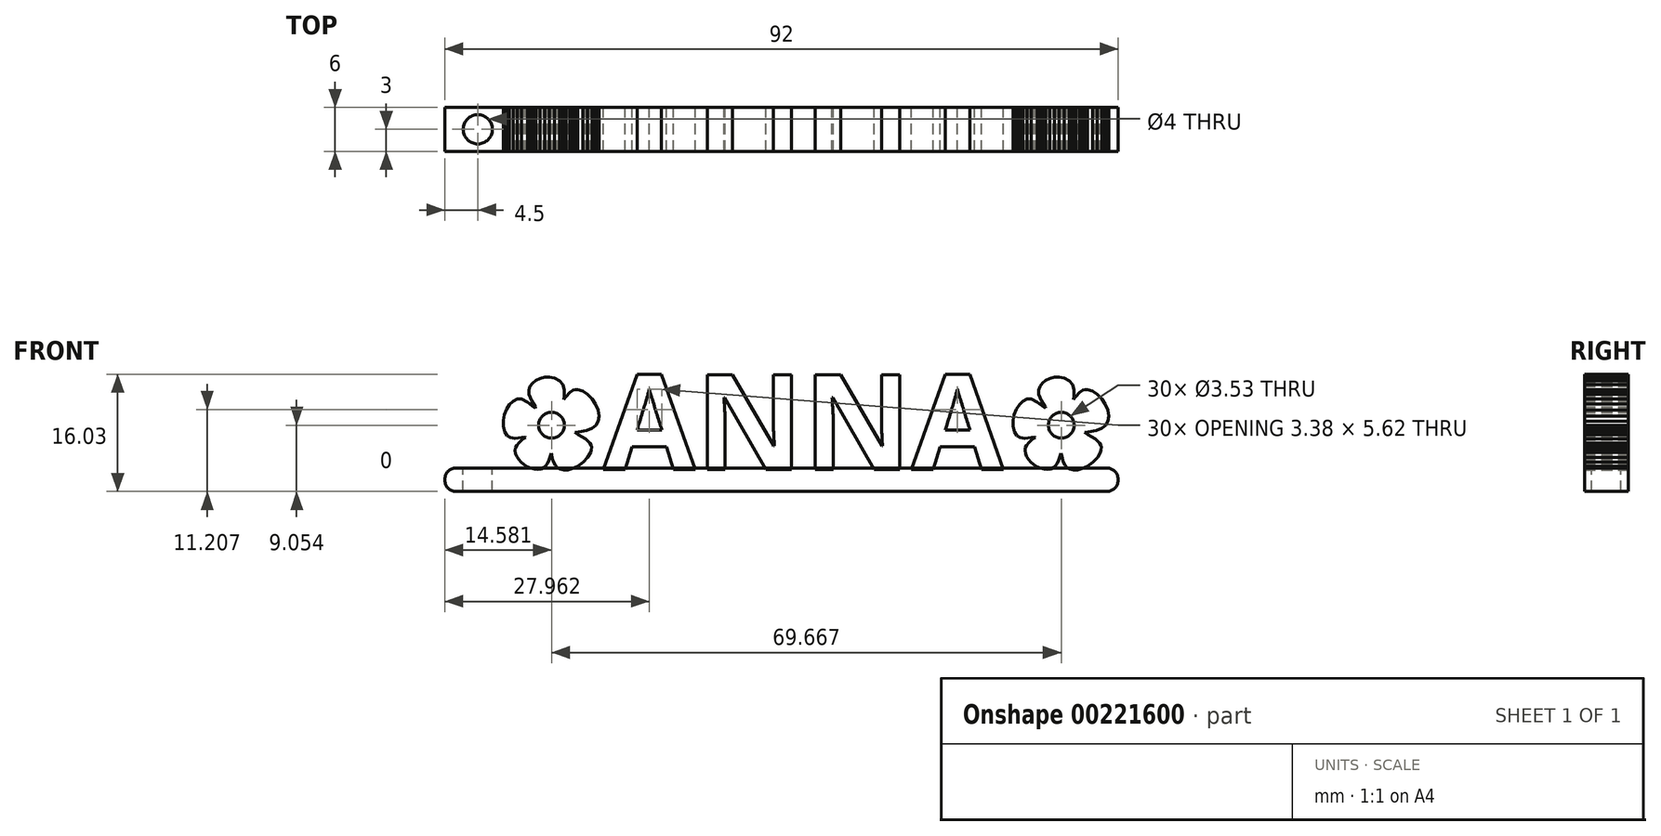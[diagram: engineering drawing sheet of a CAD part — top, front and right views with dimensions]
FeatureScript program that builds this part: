
annotation { "Feature Type Name" : "Feature", "Feature Type Description" : "" }
export const myFeature = defineFeature(function(context is Context, id is Id, definition is map)
    precondition{}
    {
        {
            var Q0;
            Q0=qCreatedBy(makeId("Front.planeOp"),FACE);
            var sketch = newSketch(context, id + "F0", { "sketchPlane" : qUnion([Q0])});
            skText(sketch, "E0", { "text": "   ANNA", "fontName": "OpenSans-Bold.ttf"});
            skLineSegment(sketch, "E1.0.0", {"start": v(-9.3, 0.1) * mm, "end": v(-8.53, 0.46) * mm});
            skLineSegment(sketch, "E1.0.1", {"start": v(-8.53, 0.46) * mm, "end": v(-7.79, 1.02) * mm});
            skLineSegment(sketch, "E1.0.2", {"start": v(-7.79, 1.02) * mm, "end": v(-7.18, 1.67) * mm});
            skLineSegment(sketch, "E1.0.3", {"start": v(-7.18, 1.67) * mm, "end": v(-6.78, 2.35) * mm});
            skLineSegment(sketch, "E1.0.4", {"start": v(-6.78, 2.35) * mm, "end": v(-6.68, 2.7) * mm});
            skLineSegment(sketch, "E1.0.5", {"start": v(-6.68, 2.7) * mm, "end": v(-6.67, 3.02) * mm});
            skLineSegment(sketch, "E1.0.6", {"start": v(-6.67, 3.02) * mm, "end": v(-6.73, 3.33) * mm});
            skLineSegment(sketch, "E1.0.7", {"start": v(-6.73, 3.33) * mm, "end": v(-6.89, 3.62) * mm});
            skLineSegment(sketch, "E1.0.8", {"start": v(-6.89, 3.62) * mm, "end": v(-7.48, 4.2) * mm});
            skLineSegment(sketch, "E1.0.9", {"start": v(-7.48, 4.2) * mm, "end": v(-8.5, 4.79) * mm});
            skLineSegment(sketch, "E1.0.10", {"start": v(-8.5, 4.79) * mm, "end": v(-8.93, 5.06) * mm});
            skLineSegment(sketch, "E1.0.11", {"start": v(-8.93, 5.06) * mm, "end": v(-8.42, 5.16) * mm});
            skLineSegment(sketch, "E1.0.12", {"start": v(-8.42, 5.16) * mm, "end": v(-7.31, 5.37) * mm});
            skLineSegment(sketch, "E1.0.13", {"start": v(-7.31, 5.37) * mm, "end": v(-6.55, 5.65) * mm});
            skLineSegment(sketch, "E1.0.14", {"start": v(-6.55, 5.65) * mm, "end": v(-6.05, 6.04) * mm});
            skLineSegment(sketch, "E1.0.15", {"start": v(-6.05, 6.04) * mm, "end": v(-5.76, 6.58) * mm});
            skLineSegment(sketch, "E1.0.16", {"start": v(-5.76, 6.58) * mm, "end": v(-5.64, 7.33) * mm});
            skLineSegment(sketch, "E1.0.17", {"start": v(-5.64, 7.33) * mm, "end": v(-5.78, 8.14) * mm});
            skLineSegment(sketch, "E1.0.18", {"start": v(-5.78, 8.14) * mm, "end": v(-6.1, 8.93) * mm});
            skLineSegment(sketch, "E1.0.19", {"start": v(-6.1, 8.93) * mm, "end": v(-6.6, 9.67) * mm});
            skLineSegment(sketch, "E1.0.20", {"start": v(-6.6, 9.67) * mm, "end": v(-7.2, 10.28) * mm});
            skLineSegment(sketch, "E1.0.21", {"start": v(-7.2, 10.28) * mm, "end": v(-7.86, 10.72) * mm});
            skLineSegment(sketch, "E1.0.22", {"start": v(-7.86, 10.72) * mm, "end": v(-8.55, 10.93) * mm});
            skLineSegment(sketch, "E1.0.23", {"start": v(-8.55, 10.93) * mm, "end": v(-8.88, 10.93) * mm});
            skLineSegment(sketch, "E1.0.24", {"start": v(-8.88, 10.93) * mm, "end": v(-9.2, 10.85) * mm});
            skLineSegment(sketch, "E1.0.25", {"start": v(-9.2, 10.85) * mm, "end": v(-9.65, 10.56) * mm});
            skLineSegment(sketch, "E1.0.26", {"start": v(-9.65, 10.56) * mm, "end": v(-10.14, 9.98) * mm});
            skLineSegment(sketch, "E1.0.27", {"start": v(-10.14, 9.98) * mm, "end": v(-10.45, 9.58) * mm});
            skLineSegment(sketch, "E1.0.28", {"start": v(-10.45, 9.58) * mm, "end": v(-10.4, 10.03) * mm});
            skLineSegment(sketch, "E1.0.29", {"start": v(-10.4, 10.03) * mm, "end": v(-10.4, 10.93) * mm});
            skLineSegment(sketch, "E1.0.30", {"start": v(-10.4, 10.93) * mm, "end": v(-10.6, 11.63) * mm});
            skLineSegment(sketch, "E1.0.31", {"start": v(-10.6, 11.63) * mm, "end": v(-11.04, 12.15) * mm});
            skLineSegment(sketch, "E1.0.32", {"start": v(-11.04, 12.15) * mm, "end": v(-11.71, 12.5) * mm});
            skLineSegment(sketch, "E1.0.33", {"start": v(-11.71, 12.5) * mm, "end": v(-12.4, 12.64) * mm});
            skLineSegment(sketch, "E1.0.34", {"start": v(-12.4, 12.64) * mm, "end": v(-13.07, 12.62) * mm});
            skLineSegment(sketch, "E1.0.35", {"start": v(-13.07, 12.62) * mm, "end": v(-13.7, 12.47) * mm});
            skLineSegment(sketch, "E1.0.36", {"start": v(-13.7, 12.47) * mm, "end": v(-14.26, 12.2) * mm});
            skLineSegment(sketch, "E1.0.37", {"start": v(-14.26, 12.2) * mm, "end": v(-14.72, 11.83) * mm});
            skLineSegment(sketch, "E1.0.38", {"start": v(-14.72, 11.83) * mm, "end": v(-15.05, 11.38) * mm});
            skLineSegment(sketch, "E1.0.39", {"start": v(-15.05, 11.38) * mm, "end": v(-15.22, 10.87) * mm});
            skLineSegment(sketch, "E1.0.40", {"start": v(-15.22, 10.87) * mm, "end": v(-15.2, 10.3) * mm});
            skLineSegment(sketch, "E1.0.41", {"start": v(-15.2, 10.3) * mm, "end": v(-14.83, 9.4) * mm});
            skLineSegment(sketch, "E1.0.42", {"start": v(-14.83, 9.4) * mm, "end": v(-14.35, 8.55) * mm});
            skLineSegment(sketch, "E1.0.43", {"start": v(-14.35, 8.55) * mm, "end": v(-14.3, 8.4) * mm});
            skLineSegment(sketch, "E1.0.44", {"start": v(-14.3, 8.4) * mm, "end": v(-14.48, 8.53) * mm});
            skLineSegment(sketch, "E1.0.45", {"start": v(-14.48, 8.53) * mm, "end": v(-15.4, 9.23) * mm});
            skLineSegment(sketch, "E1.0.46", {"start": v(-15.4, 9.23) * mm, "end": v(-16.22, 9.63) * mm});
            skLineSegment(sketch, "E1.0.47", {"start": v(-16.22, 9.63) * mm, "end": v(-16.8, 9.63) * mm});
            skLineSegment(sketch, "E1.0.48", {"start": v(-16.8, 9.63) * mm, "end": v(-17.36, 9.37) * mm});
            skLineSegment(sketch, "E1.0.49", {"start": v(-17.36, 9.37) * mm, "end": v(-17.85, 8.9) * mm});
            skLineSegment(sketch, "E1.0.50", {"start": v(-17.85, 8.9) * mm, "end": v(-18.26, 8.26) * mm});
            skLineSegment(sketch, "E1.0.51", {"start": v(-18.26, 8.26) * mm, "end": v(-18.56, 7.51) * mm});
            skLineSegment(sketch, "E1.0.52", {"start": v(-18.56, 7.51) * mm, "end": v(-18.72, 6.71) * mm});
            skLineSegment(sketch, "E1.0.53", {"start": v(-18.72, 6.71) * mm, "end": v(-18.72, 5.9) * mm});
            skLineSegment(sketch, "E1.0.54", {"start": v(-18.72, 5.9) * mm, "end": v(-18.52, 5.16) * mm});
            skLineSegment(sketch, "E1.0.55", {"start": v(-18.52, 5.16) * mm, "end": v(-18.2, 4.64) * mm});
            skLineSegment(sketch, "E1.0.56", {"start": v(-18.2, 4.64) * mm, "end": v(-17.75, 4.36) * mm});
            skLineSegment(sketch, "E1.0.57", {"start": v(-17.75, 4.36) * mm, "end": v(-17.1, 4.27) * mm});
            skLineSegment(sketch, "E1.0.58", {"start": v(-17.1, 4.27) * mm, "end": v(-16.21, 4.37) * mm});
            skLineSegment(sketch, "E1.0.59", {"start": v(-16.21, 4.37) * mm, "end": v(-15.7, 4.43) * mm});
            skLineSegment(sketch, "E1.0.60", {"start": v(-15.7, 4.43) * mm, "end": v(-15.67, 4.4) * mm});
            skLineSegment(sketch, "E1.0.61", {"start": v(-15.67, 4.4) * mm, "end": v(-15.78, 4.33) * mm});
            skLineSegment(sketch, "E1.0.62", {"start": v(-15.78, 4.33) * mm, "end": v(-16.17, 4.07) * mm});
            skLineSegment(sketch, "E1.0.63", {"start": v(-16.17, 4.07) * mm, "end": v(-16.55, 3.71) * mm});
            skLineSegment(sketch, "E1.0.64", {"start": v(-16.55, 3.71) * mm, "end": v(-16.87, 3.33) * mm});
            skLineSegment(sketch, "E1.0.65", {"start": v(-16.87, 3.33) * mm, "end": v(-17.04, 3) * mm});
            skLineSegment(sketch, "E1.0.66", {"start": v(-17.04, 3) * mm, "end": v(-17.08, 2.6) * mm});
            skLineSegment(sketch, "E1.0.67", {"start": v(-17.08, 2.6) * mm, "end": v(-17.02, 2.2) * mm});
            skLineSegment(sketch, "E1.0.68", {"start": v(-17.02, 2.2) * mm, "end": v(-16.87, 1.78) * mm});
            skLineSegment(sketch, "E1.0.69", {"start": v(-16.87, 1.78) * mm, "end": v(-16.62, 1.39) * mm});
            skLineSegment(sketch, "E1.0.70", {"start": v(-16.62, 1.39) * mm, "end": v(-16.3, 1.02) * mm});
            skLineSegment(sketch, "E1.0.71", {"start": v(-16.3, 1.02) * mm, "end": v(-15.9, 0.69) * mm});
            skLineSegment(sketch, "E1.0.72", {"start": v(-15.9, 0.69) * mm, "end": v(-15.45, 0.4) * mm});
            skLineSegment(sketch, "E1.0.73", {"start": v(-15.45, 0.4) * mm, "end": v(-14.95, 0.2) * mm});
            skLineSegment(sketch, "E1.0.74", {"start": v(-14.95, 0.2) * mm, "end": v(-14.44, 0.06) * mm});
            skLineSegment(sketch, "E1.0.75", {"start": v(-14.44, 0.06) * mm, "end": v(-13.98, 0.02) * mm});
            skLineSegment(sketch, "E1.0.76", {"start": v(-13.98, 0.02) * mm, "end": v(-13.58, 0.08) * mm});
            skLineSegment(sketch, "E1.0.77", {"start": v(-13.58, 0.08) * mm, "end": v(-13.23, 0.23) * mm});
            skLineSegment(sketch, "E1.0.78", {"start": v(-13.23, 0.23) * mm, "end": v(-12.92, 0.49) * mm});
            skLineSegment(sketch, "E1.0.79", {"start": v(-12.92, 0.49) * mm, "end": v(-12.67, 0.84) * mm});
            skLineSegment(sketch, "E1.0.80", {"start": v(-12.67, 0.84) * mm, "end": v(-12.46, 1.28) * mm});
            skLineSegment(sketch, "E1.0.81", {"start": v(-12.46, 1.28) * mm, "end": v(-12.3, 1.83) * mm});
            skLineSegment(sketch, "E1.0.82", {"start": v(-12.3, 1.83) * mm, "end": v(-12.19, 2.26) * mm});
            skLineSegment(sketch, "E1.0.83", {"start": v(-12.19, 2.26) * mm, "end": v(-12.13, 2.1) * mm});
            skLineSegment(sketch, "E1.0.84", {"start": v(-12.13, 2.1) * mm, "end": v(-12.01, 1.53) * mm});
            skLineSegment(sketch, "E1.0.85", {"start": v(-12.01, 1.53) * mm, "end": v(-11.82, 1) * mm});
            skLineSegment(sketch, "E1.0.86", {"start": v(-11.82, 1) * mm, "end": v(-11.6, 0.55) * mm});
            skLineSegment(sketch, "E1.0.87", {"start": v(-11.6, 0.55) * mm, "end": v(-11.35, 0.26) * mm});
            skLineSegment(sketch, "E1.0.88", {"start": v(-11.35, 0.26) * mm, "end": v(-10.95, 0.05) * mm});
            skLineSegment(sketch, "E1.0.89", {"start": v(-10.95, 0.05) * mm, "end": v(-10.46, -0.04) * mm});
            skLineSegment(sketch, "E1.0.90", {"start": v(-10.46, -0.04) * mm, "end": v(-9.9, -0.03) * mm});
            skLineSegment(sketch, "E1.0.91", {"start": v(-9.9, -0.03) * mm, "end": v(-9.3, 0.1) * mm});
            skCircle(sketch, "E2", {"center": v(-12.12, 6.05) * mm, "radius": 1.77 * mm});
            skCircle(sketch, "E3.1.0.0", {"center": v(57.55, 6.05) * mm, "radius": 1.77 * mm});
            skLineSegment(sketch, "E3.1.0.1", {"start": v(59.22, 9.58) * mm, "end": v(59.26, 10.03) * mm});
            skLineSegment(sketch, "E3.1.0.2", {"start": v(62.47, 10.28) * mm, "end": v(61.8, 10.72) * mm});
            skLineSegment(sketch, "E3.1.0.3", {"start": v(50.95, 5.9) * mm, "end": v(51.15, 5.16) * mm});
            skLineSegment(sketch, "E3.1.0.4", {"start": v(55.4, 12.2) * mm, "end": v(54.94, 11.83) * mm});
            skLineSegment(sketch, "E3.1.0.5", {"start": v(53.37, 1.02) * mm, "end": v(53.76, 0.69) * mm});
            skLineSegment(sketch, "E3.1.0.6", {"start": v(53.45, 9.63) * mm, "end": v(52.86, 9.63) * mm});
            skLineSegment(sketch, "E3.1.0.7", {"start": v(51.1, 7.51) * mm, "end": v(50.95, 6.71) * mm});
            skLineSegment(sketch, "E3.1.0.8", {"start": v(54.27, 9.23) * mm, "end": v(53.45, 9.63) * mm});
            skLineSegment(sketch, "E3.1.0.9", {"start": v(52.86, 9.63) * mm, "end": v(52.31, 9.37) * mm});
            skLineSegment(sketch, "E3.1.0.10", {"start": v(59.53, 9.98) * mm, "end": v(59.22, 9.58) * mm});
            skLineSegment(sketch, "E3.1.0.11", {"start": v(59.07, 11.63) * mm, "end": v(58.63, 12.15) * mm});
            skLineSegment(sketch, "E3.1.0.12", {"start": v(58.63, 12.15) * mm, "end": v(57.95, 12.5) * mm});
            skLineSegment(sketch, "E3.1.0.13", {"start": v(59.28, 10.93) * mm, "end": v(59.07, 11.63) * mm});
            skLineSegment(sketch, "E3.1.0.14", {"start": v(54.21, 0.4) * mm, "end": v(54.72, 0.2) * mm});
            skLineSegment(sketch, "E3.1.0.15", {"start": v(59.77, -0.03) * mm, "end": v(60.36, 0.1) * mm});
            skLineSegment(sketch, "E3.1.0.16", {"start": v(50.95, 6.71) * mm, "end": v(50.95, 5.9) * mm});
            skLineSegment(sketch, "E3.1.0.17", {"start": v(60.36, 0.1) * mm, "end": v(61.14, 0.46) * mm});
            skLineSegment(sketch, "E3.1.0.18", {"start": v(53.76, 0.69) * mm, "end": v(54.21, 0.4) * mm});
            skLineSegment(sketch, "E3.1.0.19", {"start": v(51.15, 5.16) * mm, "end": v(51.47, 4.64) * mm});
            skLineSegment(sketch, "E3.1.0.20", {"start": v(62.35, 5.37) * mm, "end": v(63.12, 5.65) * mm});
            skLineSegment(sketch, "E3.1.0.21", {"start": v(61.14, 0.46) * mm, "end": v(61.88, 1.02) * mm});
            skLineSegment(sketch, "E3.1.0.22", {"start": v(63.07, 9.67) * mm, "end": v(62.47, 10.28) * mm});
            skLineSegment(sketch, "E3.1.0.23", {"start": v(59.26, 10.03) * mm, "end": v(59.28, 10.93) * mm});
            skLineSegment(sketch, "E3.1.0.24", {"start": v(52.31, 9.37) * mm, "end": v(51.81, 8.9) * mm});
            skLineSegment(sketch, "E3.1.0.25", {"start": v(57.95, 12.5) * mm, "end": v(57.27, 12.64) * mm});
            skLineSegment(sketch, "E3.1.0.26", {"start": v(56.6, 12.62) * mm, "end": v(55.96, 12.47) * mm});
            skLineSegment(sketch, "E3.1.0.27", {"start": v(62.5, 1.67) * mm, "end": v(62.88, 2.35) * mm});
            skLineSegment(sketch, "E3.1.0.28", {"start": v(63.56, 8.93) * mm, "end": v(63.07, 9.67) * mm});
            skLineSegment(sketch, "E3.1.0.29", {"start": v(57.27, 12.64) * mm, "end": v(56.6, 12.62) * mm});
            skLineSegment(sketch, "E3.1.0.30", {"start": v(61.88, 1.02) * mm, "end": v(62.5, 1.67) * mm});
            skLineSegment(sketch, "E3.1.0.31", {"start": v(51.81, 8.9) * mm, "end": v(51.4, 8.26) * mm});
            skLineSegment(sketch, "E3.1.0.32", {"start": v(51.4, 8.26) * mm, "end": v(51.1, 7.51) * mm});
            skLineSegment(sketch, "E3.1.0.33", {"start": v(55.96, 12.47) * mm, "end": v(55.4, 12.2) * mm});
            skLineSegment(sketch, "E3.1.0.34", {"start": v(62.88, 2.35) * mm, "end": v(62.98, 2.7) * mm});
            skLineSegment(sketch, "E3.1.0.35", {"start": v(52.86, 9.63) * mm, "end": v(52.31, 9.37) * mm});
            skLineSegment(sketch, "E3.1.0.36", {"start": v(57.27, 12.64) * mm, "end": v(56.6, 12.62) * mm});
            skLineSegment(sketch, "E3.1.0.37", {"start": v(62.35, 5.37) * mm, "end": v(63.12, 5.65) * mm});
            skLineSegment(sketch, "E3.1.0.38", {"start": v(58.71, 0.05) * mm, "end": v(59.21, -0.04) * mm});
            skLineSegment(sketch, "E3.1.0.39", {"start": v(63.56, 8.93) * mm, "end": v(63.07, 9.67) * mm});
            skLineSegment(sketch, "E3.1.0.40", {"start": v(59.77, -0.03) * mm, "end": v(60.36, 0.1) * mm});
            skLineSegment(sketch, "E3.1.0.41", {"start": v(59.53, 9.98) * mm, "end": v(59.22, 9.58) * mm});
            skLineSegment(sketch, "E3.1.0.42", {"start": v(61.88, 1.02) * mm, "end": v(62.5, 1.67) * mm});
            skLineSegment(sketch, "E3.1.0.43", {"start": v(62.88, 2.35) * mm, "end": v(62.98, 2.7) * mm});
            skLineSegment(sketch, "E3.1.0.44", {"start": v(50.95, 6.71) * mm, "end": v(50.95, 5.9) * mm});
            skLineSegment(sketch, "E3.1.0.45", {"start": v(60.36, 0.1) * mm, "end": v(61.14, 0.46) * mm});
            skLineSegment(sketch, "E3.1.0.46", {"start": v(56.6, 12.62) * mm, "end": v(55.96, 12.47) * mm});
            skLineSegment(sketch, "E3.1.0.47", {"start": v(55.4, 12.2) * mm, "end": v(54.94, 11.83) * mm});
            skLineSegment(sketch, "E3.1.0.48", {"start": v(54.21, 0.4) * mm, "end": v(54.72, 0.2) * mm});
            skLineSegment(sketch, "E3.1.0.49", {"start": v(59.26, 10.03) * mm, "end": v(59.28, 10.93) * mm});
            skLineSegment(sketch, "E3.1.0.50", {"start": v(59.22, 9.58) * mm, "end": v(59.26, 10.03) * mm});
            skLineSegment(sketch, "E3.1.0.51", {"start": v(59.21, -0.04) * mm, "end": v(59.77, -0.03) * mm});
            skLineSegment(sketch, "E3.1.0.52", {"start": v(53.45, 9.63) * mm, "end": v(52.86, 9.63) * mm});
            skLineSegment(sketch, "E3.1.0.53", {"start": v(59.28, 10.93) * mm, "end": v(59.07, 11.63) * mm});
            skLineSegment(sketch, "E3.1.0.54", {"start": v(62.47, 10.28) * mm, "end": v(61.8, 10.72) * mm});
            skLineSegment(sketch, "E3.1.0.55", {"start": v(51.81, 8.9) * mm, "end": v(51.4, 8.26) * mm});
            skLineSegment(sketch, "E3.1.0.56", {"start": v(53.76, 0.69) * mm, "end": v(54.21, 0.4) * mm});
            skLineSegment(sketch, "E3.1.0.57", {"start": v(57.95, 12.5) * mm, "end": v(57.27, 12.64) * mm});
            skLineSegment(sketch, "E3.1.0.58", {"start": v(52.31, 9.37) * mm, "end": v(51.81, 8.9) * mm});
            skLineSegment(sketch, "E3.1.0.59", {"start": v(50.95, 5.9) * mm, "end": v(51.15, 5.16) * mm});
            skLineSegment(sketch, "E3.1.0.60", {"start": v(58.63, 12.15) * mm, "end": v(57.95, 12.5) * mm});
            skLineSegment(sketch, "E3.1.0.61", {"start": v(54.27, 9.23) * mm, "end": v(53.45, 9.63) * mm});
            skLineSegment(sketch, "E3.1.0.62", {"start": v(61.14, 0.46) * mm, "end": v(61.88, 1.02) * mm});
            skLineSegment(sketch, "E3.1.0.63", {"start": v(59.07, 11.63) * mm, "end": v(58.63, 12.15) * mm});
            skLineSegment(sketch, "E3.1.0.64", {"start": v(51.4, 8.26) * mm, "end": v(51.1, 7.51) * mm});
            skLineSegment(sketch, "E3.1.0.65", {"start": v(62.5, 1.67) * mm, "end": v(62.88, 2.35) * mm});
            skLineSegment(sketch, "E3.1.0.66", {"start": v(51.1, 7.51) * mm, "end": v(50.95, 6.71) * mm});
            skLineSegment(sketch, "E3.1.0.67", {"start": v(53.37, 1.02) * mm, "end": v(53.76, 0.69) * mm});
            skLineSegment(sketch, "E3.1.0.68", {"start": v(51.15, 5.16) * mm, "end": v(51.47, 4.64) * mm});
            skLineSegment(sketch, "E3.1.0.69", {"start": v(55.96, 12.47) * mm, "end": v(55.4, 12.2) * mm});
            skLineSegment(sketch, "E3.1.0.70", {"start": v(63.07, 9.67) * mm, "end": v(62.47, 10.28) * mm});
            skLineSegment(sketch, "E3.1.0.71", {"start": v(54.94, 11.83) * mm, "end": v(54.61, 11.38) * mm});
            skLineSegment(sketch, "E3.1.0.72", {"start": v(61.8, 10.72) * mm, "end": v(61.12, 10.93) * mm});
            skLineSegment(sketch, "E3.1.0.73", {"start": v(63.61, 6.04) * mm, "end": v(63.91, 6.58) * mm});
            skLineSegment(sketch, "E3.1.0.74", {"start": v(62.98, 2.7) * mm, "end": v(63, 3.02) * mm});
            skLineSegment(sketch, "E3.1.0.75", {"start": v(61.12, 10.93) * mm, "end": v(60.79, 10.93) * mm});
            skLineSegment(sketch, "E3.1.0.76", {"start": v(51.47, 4.64) * mm, "end": v(51.92, 4.36) * mm});
            skLineSegment(sketch, "E3.1.0.77", {"start": v(60.46, 10.85) * mm, "end": v(60.02, 10.56) * mm});
            skLineSegment(sketch, "E3.1.0.78", {"start": v(61.25, 5.16) * mm, "end": v(62.35, 5.37) * mm});
            skLineSegment(sketch, "E3.1.0.79", {"start": v(63, 3.02) * mm, "end": v(62.94, 3.33) * mm});
            skLineSegment(sketch, "E3.1.0.80", {"start": v(62.94, 3.33) * mm, "end": v(62.78, 3.62) * mm});
            skLineSegment(sketch, "E3.1.0.81", {"start": v(62.18, 4.2) * mm, "end": v(61.17, 4.79) * mm});
            skLineSegment(sketch, "E3.1.0.82", {"start": v(64.02, 7.33) * mm, "end": v(63.9, 8.14) * mm});
            skLineSegment(sketch, "E3.1.0.83", {"start": v(53.04, 1.39) * mm, "end": v(53.37, 1.02) * mm});
            skLineSegment(sketch, "E3.1.0.84", {"start": v(55.23, 0.06) * mm, "end": v(55.68, 0.02) * mm});
            skLineSegment(sketch, "E3.1.0.85", {"start": v(60.74, 5.06) * mm, "end": v(61.25, 5.16) * mm});
            skLineSegment(sketch, "E3.1.0.86", {"start": v(58.31, 0.26) * mm, "end": v(58.71, 0.05) * mm});
            skLineSegment(sketch, "E3.1.0.87", {"start": v(54.61, 11.38) * mm, "end": v(54.45, 10.87) * mm});
            skLineSegment(sketch, "E3.1.0.88", {"start": v(63.91, 6.58) * mm, "end": v(64.02, 7.33) * mm});
            skLineSegment(sketch, "E3.1.0.89", {"start": v(58.71, 0.05) * mm, "end": v(59.21, -0.04) * mm});
            skLineSegment(sketch, "E3.1.0.90", {"start": v(61.17, 4.79) * mm, "end": v(60.74, 5.06) * mm});
            skLineSegment(sketch, "E3.1.0.91", {"start": v(54.72, 0.2) * mm, "end": v(55.23, 0.06) * mm});
            skLineSegment(sketch, "E3.1.0.92", {"start": v(54.47, 10.3) * mm, "end": v(54.84, 9.4) * mm});
            skLineSegment(sketch, "E3.1.0.93", {"start": v(52.8, 1.78) * mm, "end": v(53.04, 1.39) * mm});
            skLineSegment(sketch, "E3.1.0.94", {"start": v(62.78, 3.62) * mm, "end": v(62.18, 4.2) * mm});
            skLineSegment(sketch, "E3.1.0.95", {"start": v(59.21, -0.04) * mm, "end": v(59.77, -0.03) * mm});
            skLineSegment(sketch, "E3.1.0.96", {"start": v(54.45, 10.87) * mm, "end": v(54.47, 10.3) * mm});
            skLineSegment(sketch, "E3.1.0.97", {"start": v(63.12, 5.65) * mm, "end": v(63.61, 6.04) * mm});
            skLineSegment(sketch, "E3.1.0.98", {"start": v(60.79, 10.93) * mm, "end": v(60.46, 10.85) * mm});
            skLineSegment(sketch, "E3.1.0.99", {"start": v(60.02, 10.56) * mm, "end": v(59.53, 9.98) * mm});
            skLineSegment(sketch, "E3.1.0.100", {"start": v(55.68, 0.02) * mm, "end": v(56.09, 0.08) * mm});
            skLineSegment(sketch, "E3.1.0.101", {"start": v(52.64, 2.2) * mm, "end": v(52.8, 1.78) * mm});
            skLineSegment(sketch, "E3.1.0.102", {"start": v(63.9, 8.14) * mm, "end": v(63.56, 8.93) * mm});
            skLineSegment(sketch, "E3.1.0.103", {"start": v(61.17, 4.79) * mm, "end": v(60.74, 5.06) * mm});
            skLineSegment(sketch, "E3.1.0.104", {"start": v(60.74, 5.06) * mm, "end": v(61.25, 5.16) * mm});
            skLineSegment(sketch, "E3.1.0.105", {"start": v(51.47, 4.64) * mm, "end": v(51.92, 4.36) * mm});
            skLineSegment(sketch, "E3.1.0.106", {"start": v(58.07, 0.55) * mm, "end": v(58.31, 0.26) * mm});
            skLineSegment(sketch, "E3.1.0.107", {"start": v(58.31, 0.26) * mm, "end": v(58.71, 0.05) * mm});
            skLineSegment(sketch, "E3.1.0.108", {"start": v(52.8, 1.78) * mm, "end": v(53.04, 1.39) * mm});
            skLineSegment(sketch, "E3.1.0.109", {"start": v(62.78, 3.62) * mm, "end": v(62.18, 4.2) * mm});
            skLineSegment(sketch, "E3.1.0.110", {"start": v(61.25, 5.16) * mm, "end": v(62.35, 5.37) * mm});
            skLineSegment(sketch, "E3.1.0.111", {"start": v(54.47, 10.3) * mm, "end": v(54.84, 9.4) * mm});
            skLineSegment(sketch, "E3.1.0.112", {"start": v(63.12, 5.65) * mm, "end": v(63.61, 6.04) * mm});
            skLineSegment(sketch, "E3.1.0.113", {"start": v(60.02, 10.56) * mm, "end": v(59.53, 9.98) * mm});
            skLineSegment(sketch, "E3.1.0.114", {"start": v(63.91, 6.58) * mm, "end": v(64.02, 7.33) * mm});
            skLineSegment(sketch, "E3.1.0.115", {"start": v(54.45, 10.87) * mm, "end": v(54.47, 10.3) * mm});
            skLineSegment(sketch, "E3.1.0.116", {"start": v(60.79, 10.93) * mm, "end": v(60.46, 10.85) * mm});
            skLineSegment(sketch, "E3.1.0.117", {"start": v(55.68, 0.02) * mm, "end": v(56.09, 0.08) * mm});
            skLineSegment(sketch, "E3.1.0.118", {"start": v(60.46, 10.85) * mm, "end": v(60.02, 10.56) * mm});
            skLineSegment(sketch, "E3.1.0.119", {"start": v(55.23, 0.06) * mm, "end": v(55.68, 0.02) * mm});
            skLineSegment(sketch, "E3.1.0.120", {"start": v(54.72, 0.2) * mm, "end": v(55.23, 0.06) * mm});
            skLineSegment(sketch, "E3.1.0.121", {"start": v(62.18, 4.2) * mm, "end": v(61.17, 4.79) * mm});
            skLineSegment(sketch, "E3.1.0.122", {"start": v(63.61, 6.04) * mm, "end": v(63.91, 6.58) * mm});
            skLineSegment(sketch, "E3.1.0.123", {"start": v(52.58, 2.6) * mm, "end": v(52.64, 2.2) * mm});
            skLineSegment(sketch, "E3.1.0.124", {"start": v(62.98, 2.7) * mm, "end": v(63, 3.02) * mm});
            skLineSegment(sketch, "E3.1.0.125", {"start": v(53.04, 1.39) * mm, "end": v(53.37, 1.02) * mm});
            skLineSegment(sketch, "E3.1.0.126", {"start": v(63.9, 8.14) * mm, "end": v(63.56, 8.93) * mm});
            skLineSegment(sketch, "E3.1.0.127", {"start": v(64.02, 7.33) * mm, "end": v(63.9, 8.14) * mm});
            skLineSegment(sketch, "E3.1.0.128", {"start": v(63, 3.02) * mm, "end": v(62.94, 3.33) * mm});
            skLineSegment(sketch, "E3.1.0.129", {"start": v(52.64, 2.2) * mm, "end": v(52.8, 1.78) * mm});
            skLineSegment(sketch, "E3.1.0.130", {"start": v(62.94, 3.33) * mm, "end": v(62.78, 3.62) * mm});
            skLineSegment(sketch, "E3.1.0.131", {"start": v(54.61, 11.38) * mm, "end": v(54.45, 10.87) * mm});
            skLineSegment(sketch, "E3.1.0.132", {"start": v(61.12, 10.93) * mm, "end": v(60.79, 10.93) * mm});
            skLineSegment(sketch, "E3.1.0.133", {"start": v(61.8, 10.72) * mm, "end": v(61.12, 10.93) * mm});
            skLineSegment(sketch, "E3.1.0.134", {"start": v(54.94, 11.83) * mm, "end": v(54.61, 11.38) * mm});
            skLineSegment(sketch, "E3.1.0.135", {"start": v(52.58, 2.6) * mm, "end": v(52.64, 2.2) * mm});
            skLineSegment(sketch, "E3.1.0.136", {"start": v(53.45, 4.37) * mm, "end": v(53.96, 4.43) * mm});
            skLineSegment(sketch, "E3.1.0.137", {"start": v(57.66, 1.53) * mm, "end": v(57.84, 1) * mm});
            skLineSegment(sketch, "E3.1.0.138", {"start": v(53.89, 4.33) * mm, "end": v(53.5, 4.07) * mm});
            skLineSegment(sketch, "E3.1.0.139", {"start": v(56.44, 0.23) * mm, "end": v(56.74, 0.49) * mm});
            skLineSegment(sketch, "E3.1.0.140", {"start": v(57, 0.84) * mm, "end": v(57.2, 1.28) * mm});
            skLineSegment(sketch, "E3.1.0.141", {"start": v(57.84, 1) * mm, "end": v(58.07, 0.55) * mm});
            skLineSegment(sketch, "E3.1.0.142", {"start": v(53.5, 4.07) * mm, "end": v(53.11, 3.71) * mm});
            skLineSegment(sketch, "E3.1.0.143", {"start": v(57.54, 2.1) * mm, "end": v(57.66, 1.53) * mm});
            skLineSegment(sketch, "E3.1.0.144", {"start": v(56.74, 0.49) * mm, "end": v(57, 0.84) * mm});
            skLineSegment(sketch, "E3.1.0.145", {"start": v(52.56, 4.27) * mm, "end": v(53.45, 4.37) * mm});
            skLineSegment(sketch, "E3.1.0.146", {"start": v(53.11, 3.71) * mm, "end": v(52.8, 3.33) * mm});
            skLineSegment(sketch, "E3.1.0.147", {"start": v(51.92, 4.36) * mm, "end": v(52.56, 4.27) * mm});
            skLineSegment(sketch, "E3.1.0.148", {"start": v(57.2, 1.28) * mm, "end": v(57.36, 1.83) * mm});
            skLineSegment(sketch, "E3.1.0.149", {"start": v(57.48, 2.26) * mm, "end": v(57.54, 2.1) * mm});
            skLineSegment(sketch, "E3.1.0.150", {"start": v(52.8, 3.33) * mm, "end": v(52.63, 3) * mm});
            skLineSegment(sketch, "E3.1.0.151", {"start": v(58.07, 0.55) * mm, "end": v(58.31, 0.26) * mm});
            skLineSegment(sketch, "E3.1.0.152", {"start": v(57.36, 1.83) * mm, "end": v(57.48, 2.26) * mm});
            skLineSegment(sketch, "E3.1.0.153", {"start": v(52.63, 3) * mm, "end": v(52.58, 2.6) * mm});
            skLineSegment(sketch, "E3.1.0.154", {"start": v(56.09, 0.08) * mm, "end": v(56.44, 0.23) * mm});
            skLineSegment(sketch, "E3.1.0.155", {"start": v(54, 4.4) * mm, "end": v(53.89, 4.33) * mm});
            skLineSegment(sketch, "E3.1.0.156", {"start": v(57.48, 2.26) * mm, "end": v(57.54, 2.1) * mm});
            skLineSegment(sketch, "E3.1.0.157", {"start": v(52.56, 4.27) * mm, "end": v(53.45, 4.37) * mm});
            skLineSegment(sketch, "E3.1.0.158", {"start": v(57.66, 1.53) * mm, "end": v(57.84, 1) * mm});
            skLineSegment(sketch, "E3.1.0.159", {"start": v(53.96, 4.43) * mm, "end": v(54, 4.4) * mm});
            skLineSegment(sketch, "E3.1.0.160", {"start": v(53.11, 3.71) * mm, "end": v(52.8, 3.33) * mm});
            skLineSegment(sketch, "E3.1.0.161", {"start": v(51.92, 4.36) * mm, "end": v(52.56, 4.27) * mm});
            skLineSegment(sketch, "E3.1.0.162", {"start": v(53.45, 4.37) * mm, "end": v(53.96, 4.43) * mm});
            skLineSegment(sketch, "E3.1.0.163", {"start": v(56.09, 0.08) * mm, "end": v(56.44, 0.23) * mm});
            skLineSegment(sketch, "E3.1.0.164", {"start": v(53.5, 4.07) * mm, "end": v(53.11, 3.71) * mm});
            skLineSegment(sketch, "E3.1.0.165", {"start": v(57.54, 2.1) * mm, "end": v(57.66, 1.53) * mm});
            skLineSegment(sketch, "E3.1.0.166", {"start": v(57.36, 1.83) * mm, "end": v(57.48, 2.26) * mm});
            skLineSegment(sketch, "E3.1.0.167", {"start": v(53.89, 4.33) * mm, "end": v(53.5, 4.07) * mm});
            skLineSegment(sketch, "E3.1.0.168", {"start": v(56.44, 0.23) * mm, "end": v(56.74, 0.49) * mm});
            skLineSegment(sketch, "E3.1.0.169", {"start": v(52.63, 3) * mm, "end": v(52.58, 2.6) * mm});
            skLineSegment(sketch, "E3.1.0.170", {"start": v(57.84, 1) * mm, "end": v(58.07, 0.55) * mm});
            skLineSegment(sketch, "E3.1.0.171", {"start": v(56.74, 0.49) * mm, "end": v(57, 0.84) * mm});
            skLineSegment(sketch, "E3.1.0.172", {"start": v(57, 0.84) * mm, "end": v(57.2, 1.28) * mm});
            skLineSegment(sketch, "E3.1.0.173", {"start": v(52.8, 3.33) * mm, "end": v(52.63, 3) * mm});
            skLineSegment(sketch, "E3.1.0.174", {"start": v(57.2, 1.28) * mm, "end": v(57.36, 1.83) * mm});
            skLineSegment(sketch, "E3.1.0.175", {"start": v(54, 4.4) * mm, "end": v(53.89, 4.33) * mm});
            skLineSegment(sketch, "E3.1.0.176", {"start": v(53.96, 4.43) * mm, "end": v(54, 4.4) * mm});
            skLineSegment(sketch, "E3.1.0.177", {"start": v(55.38, 8.4) * mm, "end": v(55.19, 8.53) * mm});
            skLineSegment(sketch, "E3.1.0.178", {"start": v(55.31, 8.55) * mm, "end": v(55.38, 8.4) * mm});
            skLineSegment(sketch, "E3.1.0.179", {"start": v(54.84, 9.4) * mm, "end": v(55.31, 8.55) * mm});
            skLineSegment(sketch, "E3.1.0.180", {"start": v(55.19, 8.53) * mm, "end": v(54.27, 9.23) * mm});
            skLineSegment(sketch, "E3.1.0.181", {"start": v(55.31, 8.55) * mm, "end": v(55.38, 8.4) * mm});
            skLineSegment(sketch, "E3.1.0.182", {"start": v(54.84, 9.4) * mm, "end": v(55.31, 8.55) * mm});
            skLineSegment(sketch, "E3.1.0.183", {"start": v(55.19, 8.53) * mm, "end": v(54.27, 9.23) * mm});
            skLineSegment(sketch, "E3.1.0.184", {"start": v(55.38, 8.4) * mm, "end": v(55.19, 8.53) * mm});
            skLineSegment(sketch, "E3.direction1", {"start": v(-16.3, 1.02) * mm, "end": v(42.4, 1.02) * mm, "construction": true});
            const initialGuessF0  = {"E0": [-0.0192, 0, 1, 0, 0.01309]};
            skSetInitialGuess(sketch, initialGuessF0);
            skSolve(sketch);
        }
        {
            var Q0;
            Q0=qSketchRegion(id+"F0",true);
            extrude(context, id + "F1", {"entities" : qUnion([Q0]), "endBound" : BoundingType.SYMMETRIC, "depth" : 6 * mm});
        }
        {
            var Q0;
            Q0=qCreatedBy(makeId("Top.planeOp"),FACE);
            var sketch = newSketch(context, id + "F2", { "sketchPlane" : qUnion([Q0])});
            skLineSegment(sketch, "E4.bottom", {"start": v(-19.2, 3) * mm, "end": v(65.3, 3) * mm});
            skLineSegment(sketch, "E4.top", {"start": v(-19.2, -3) * mm, "end": v(65.3, -3) * mm});
            skLineSegment(sketch, "E4.left", {"start": v(-19.2, 3) * mm, "end": v(-19.2, -3) * mm});
            skLineSegment(sketch, "E4.right", {"start": v(65.3, 3) * mm, "end": v(65.3, -3) * mm});
            skSolve(sketch);
        }
        {
            var Q0;
            Q0=makeQuery(id+"F2.imprint","IMPRINT",FACE,{"disambiguationData":[TD([[makeQuery(id+"F2.imprint","IMPRINT",EDGE,{"derivedFrom":sQuery(id+"F2.wireOp",EDGE,"E4.bottom")}),-1.0]])]});
            extrude(context, id + "F3", {"entities" : qUnion([Q0]), "depth" : 0.2 * mm});
        }
        {
            var Q0;
            Q0=makeQuery(id+"F3.opExtrude","CAP_FACE",FACE,{"disambiguationData":[OSD([sQuery(id+"F2.wireOp",EDGE,"E4.bottom"),sQuery(id+"F2.wireOp",EDGE,"E4.top"),sQuery(id+"F2.wireOp",EDGE,"E4.left"),sQuery(id+"F2.wireOp",EDGE,"E4.right")])],"isStart":true});
            extrude(context, id + "F4", {"entities" : qUnion([Q0]), "depth" : 3 * mm});
        }
        {
            var Q0;
            {var subQ0=sQuery(id+"F2.wireOp",EDGE,"E4.left");Q0=makeQuery(id+"FaVoHrOpcFZXiYX_6.opBoolean","MERGE",FACE,{"derivedFrom":[makeQuery(id+"F3.opExtrude","SWEPT_FACE",FACE,{"disambiguationData":[OSD([subQ0])]}),makeQuery(id+"F4.opExtrude","SWEPT_FACE",FACE,{"disambiguationData":[OSD([subQ0])]})]});}
            var sketch = newSketch(context, id + "F5", { "sketchPlane" : qUnion([Q0])});
            skLineSegment(sketch, "E5.bottom", {"start": v(-3, -3) * mm, "end": v(3, -3) * mm});
            skLineSegment(sketch, "E5.top", {"start": v(-3, 0.2) * mm, "end": v(3, 0.2) * mm});
            skLineSegment(sketch, "E5.left", {"start": v(-3, -3) * mm, "end": v(-3, 0.2) * mm});
            skLineSegment(sketch, "E5.right", {"start": v(3, -3) * mm, "end": v(3, 0.2) * mm});
            skSolve(sketch);
        }
        {
            var Q0;
            Q0=qSketchRegion(id+"F5",true);
            extrude(context, id + "F6", {"entities" : qUnion([Q0]), "operationType" : NewBodyOperationType.ADD, "depth" : 7.5 * mm});
        }
        {
            var Q0;
            Q0=makeQuery(id+"F6.opExtrude","CAP_EDGE",EDGE,{"disambiguationData":[OSD([sQuery(id+"F5.wireOp",EDGE,"E5.bottom")])],"isStart":false});
            var Q1;
            Q1=makeQuery(id+"F6.opExtrude","CAP_EDGE",EDGE,{"disambiguationData":[OSD([sQuery(id+"F5.wireOp",EDGE,"E5.top")])],"isStart":false});
            var Q2;
            Q2=makeQuery(id+"F4.opExtrude","CAP_EDGE",EDGE,{"disambiguationData":[OSD([sQuery(id+"F2.wireOp",EDGE,"E4.right")])],"isStart":false});
            fillet(context, id + "F7", {"entities" : qUnion([Q0, Q1, Q2]), "radius" : 1.5 * mm, "tangentPropagation" : true, "allowEdgeOverflow" : false});
        }
        {
            var Q0;
            {var subQ19=sQuery(id+"F2.wireOp",EDGE,"E4.top");var subQ20=sQuery(id+"F2.wireOp",EDGE,"E4.bottom");var subQ63=sQuery(id+"F0.wireOp",EDGE,"E0.sketch_text.stroke-2");var subQ66=sQuery(id+"F2.wireOp",EDGE,"E4.left");Q0=makeQuery(id+"F6.boolean.opBoolean","MERGE",FACE,{"derivedFrom":[makeQuery(id+"FaVoHrOpcFZXiYX_6.opBoolean","SPLIT",FACE,{"disambiguationData":[TD([makeQuery(id+"F1.opExtrude","SWEPT_FACE",FACE,{"disambiguationData":[OSD([subQ63])]})])],"derivedFrom":makeQuery(id+"F3.opExtrude","CAP_FACE",FACE,{"disambiguationData":[OSD([subQ20,subQ19,subQ66,sQuery(id+"F2.wireOp",EDGE,"E4.right")])],"isStart":false})}),makeQuery(id+"F6.opExtrude","SWEPT_FACE",FACE,{"disambiguationData":[OSD([sQuery(id+"F5.wireOp",EDGE,"E5.top")])]})]});}
            var sketch = newSketch(context, id + "F8", { "sketchPlane" : qUnion([Q0])});
            skCircle(sketch, "E6", {"center": v(-22.2, 0) * mm, "radius": 2 * mm});
            skSolve(sketch);
        }
        {
            var Q0;
            Q0=makeQuery(id+"F8.imprint","IMPRINT",FACE,{"disambiguationData":[TD([[makeQuery(id+"F8.imprint","IMPRINT",EDGE,{"derivedFrom":sQuery(id+"F8.wireOp",EDGE,"E6")}),1.0]])]});
            extrude(context, id + "F9", {"entities" : qUnion([Q0]), "operationType" : NewBodyOperationType.REMOVE, "oppositeDirection" : true, "depth" : 4 * mm});
        }
        {
            var Q0;
            Q0=makeQuery(id+"F3.opExtrude","CAP_EDGE",EDGE,{"disambiguationData":[OSD([sQuery(id+"F2.wireOp",EDGE,"E4.right")])],"isStart":false});
            fillet(context, id + "F10", {"entities" : qUnion([Q0]), "radius" : 1.5 * mm, "tangentPropagation" : true, "allowEdgeOverflow" : false});
        }
    });
